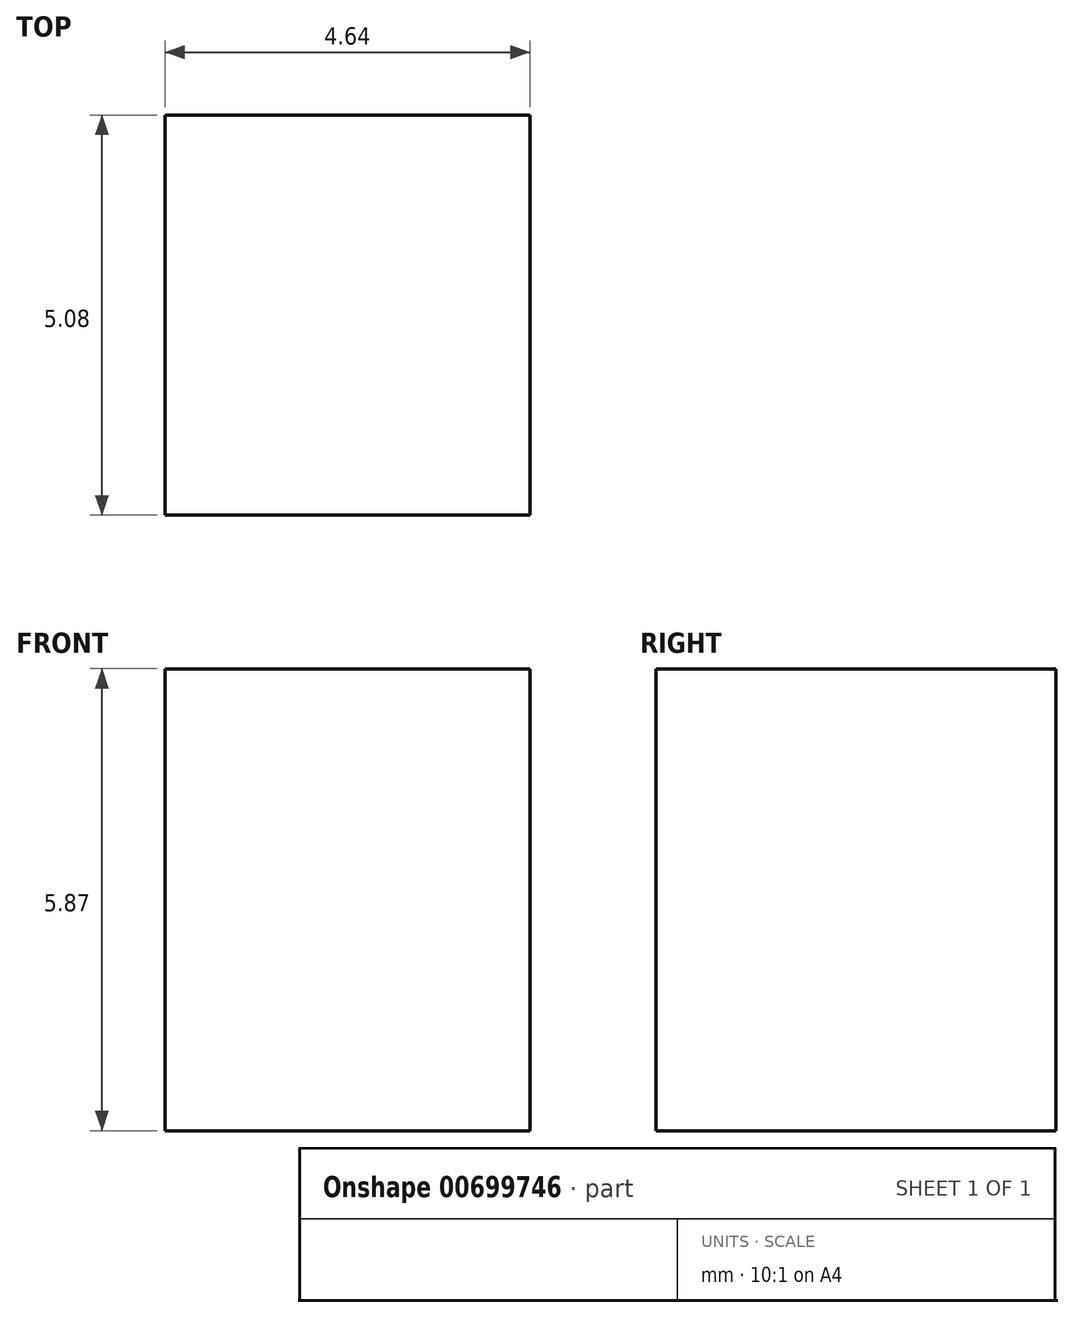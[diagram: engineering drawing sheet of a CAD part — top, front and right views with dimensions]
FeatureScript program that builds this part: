
annotation { "Feature Type Name" : "Feature", "Feature Type Description" : "" }
export const myFeature = defineFeature(function(context is Context, id is Id, definition is map)
    precondition{}
    {
        {
            var Q0;
            Q0=qCreatedBy(makeId("Front.planeOp"),FACE);
            var sketch = newSketch(context, id + "F0", { "sketchPlane" : qUnion([Q0])});
            skLineSegment(sketch, "E0.bottom", {"start": v(-146.46, 46) * mm, "end": v(-141.82, 46) * mm});
            skLineSegment(sketch, "E0.top", {"start": v(-146.46, 40.14) * mm, "end": v(-141.82, 40.14) * mm});
            skLineSegment(sketch, "E0.left", {"start": v(-146.46, 46) * mm, "end": v(-146.46, 40.14) * mm});
            skLineSegment(sketch, "E0.right", {"start": v(-141.82, 46) * mm, "end": v(-141.82, 40.14) * mm});
            skSolve(sketch);
        }
        {
            var Q0;
            Q0 = qSketchRegion(id + "F0", true);
            extrude(context, id + "F1", {"entities" : qUnion([Q0]), "depth" : 5.08 * mm, "offsetDistance" : 25.4 * mm});
        }
    });
